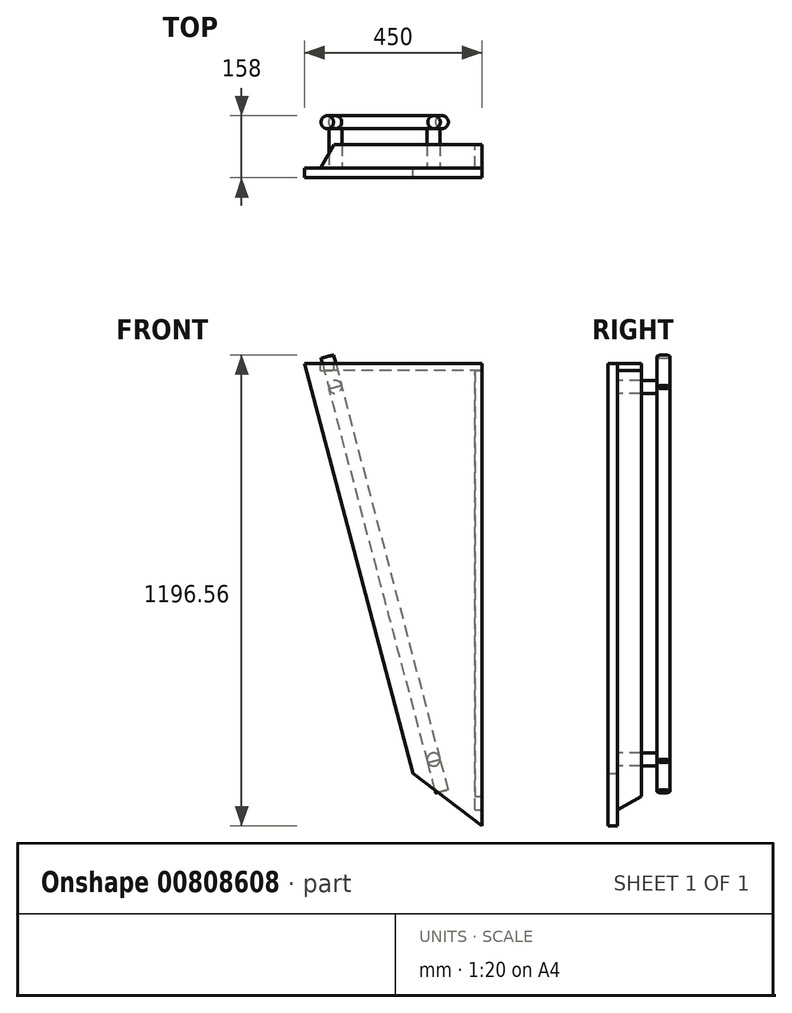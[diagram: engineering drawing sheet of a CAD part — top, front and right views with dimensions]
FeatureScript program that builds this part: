
annotation { "Feature Type Name" : "Feature", "Feature Type Description" : "" }
export const myFeature = defineFeature(function(context is Context, id is Id, definition is map)
    precondition{}
    {
        {
            var Q0;
            Q0=qCreatedBy(makeId("Front.planeOp"),FACE);
            var sketch = newSketch(context, id + "F0", { "sketchPlane" : qUnion([Q0])});
            skLineSegment(sketch, "E0", {"start": v(0, 0) * mm, "end": v(0, 1175) * mm});
            skLineSegment(sketch, "E1", {"start": v(0, 1175) * mm, "end": v(-450, 1175) * mm});
            skLineSegment(sketch, "E2", {"start": v(-450, 1175) * mm, "end": v(-175, 133.32) * mm});
            skLineSegment(sketch, "E3", {"start": v(-175, 133.32) * mm, "end": v(0, 0) * mm});
            skLineSegment(sketch, "E4", {"start": v(-175, 1175) * mm, "end": v(-175, 133.32) * mm, "construction": true});
            skSolve(sketch);
        }
        {
            var Q0;
            Q0 = qSketchRegion(id + "F0", true);
            extrude(context, id + "F1", {"entities" : qUnion([Q0]), "depth" : 25 * mm, "offsetDistance" : 25 * mm});
        }
        {
            var Q0;
            Q0=makeQuery(id+"F1.opExtrude","CAP_FACE",FACE,{"disambiguationData":[OSD([sQuery(id+"F0.wireOp",EDGE,"E0"),sQuery(id+"F0.wireOp",EDGE,"E1"),sQuery(id+"F0.wireOp",EDGE,"E2"),sQuery(id+"F0.wireOp",EDGE,"E3")])],"isStart":true});
            var sketch = newSketch(context, id + "F2", { "sketchPlane" : qUnion([Q0])});
            skLineSegment(sketch, "E5", {"start": v(372.1, 1115) * mm, "end": v(122.25, 168.56) * mm, "construction": true});
            skCircle(sketch, "E6", {"center": v(372.1, 1115) * mm, "radius": 60 * mm, "construction": true});
            skCircle(sketch, "E7", {"center": v(122.25, 168.56) * mm, "radius": 60 * mm, "construction": true});
            skCircle(sketch, "E8", {"center": v(372.1, 1115) * mm, "radius": 30 * mm});
            skCircle(sketch, "E9", {"center": v(122.25, 168.56) * mm, "radius": 30 * mm});
            skCircle(sketch, "E10", {"center": v(372.1, 1115) * mm, "radius": 16.5 * mm});
            skCircle(sketch, "E11", {"center": v(122.25, 168.56) * mm, "radius": 16.5 * mm});
            skSolve(sketch);
        }
        {
            var Q0;
            Q0=makeQuery(id+"F2.imprint","IMPRINT",FACE,{"disambiguationData":[TD([[makeQuery(id+"F2.imprint","IMPRINT",EDGE,{"derivedFrom":sQuery(id+"F2.wireOp",EDGE,"E10")}),1.0]])]});
            var Q1;
            Q1=makeQuery(id+"F2.imprint","IMPRINT",FACE,{"disambiguationData":[TD([[makeQuery(id+"F2.imprint","IMPRINT",EDGE,{"derivedFrom":sQuery(id+"F2.wireOp",EDGE,"E11")}),1.0]])]});
            extrude(context, id + "F3", {"entities" : qUnion([Q0, Q1]), "operationType" : NewBodyOperationType.ADD, "depth" : 100 * mm, "offsetDistance" : 25 * mm});
        }
        {
            var Q0;
            Q0=makeQuery(id+"F3.opExtrude","CAP_FACE",FACE,{"disambiguationData":[OSD([sQuery(id+"F2.wireOp",EDGE,"E10")])],"isStart":false});
            var sketch = newSketch(context, id + "F4", { "sketchPlane" : qUnion([Q0])});
            skLineSegment(sketch, "E12", {"start": v(372.1, 1115) * mm, "end": v(122.25, 168.56) * mm});
            skSolve(sketch);
        }
        {
            var Q0;
            Q0=sQuery(id+"F4.wireOp",VERTEX,"E12.start");
            var Q1;
            Q1=sQuery(id+"F4.wireOp",EDGE,"E12");
            cPlane(context, id + "F5", {"entities" : qUnion([Q0, Q1]), "cplaneType" : CPlaneType.LINE_POINT, "offset" : 25 * mm, "width" : 150 * mm, "height" : 150 * mm});
        }
        {
            var Q0;
            Q0=qCreatedBy(id+"F5.planeOp",FACE);
            var sketch = newSketch(context, id + "F6", { "sketchPlane" : qUnion([Q0])});
            skCircle(sketch, "E13", {"center": v(-75.17, -116.5) * mm, "radius": 16.5 * mm});
            skSolve(sketch);
        }
        {
            var Q0;
            Q0 = qSketchRegion(id + "F6", true);
            extrude(context, id + "F7", {"entities" : qUnion([Q0]), "operationType" : NewBodyOperationType.ADD, "depth" : 982.5 * mm, "offsetDistance" : 25 * mm});
        }
        {
            var Q0;
            Q0=makeQuery(id+"F7.opExtrude","CAP_FACE",FACE,{"disambiguationData":[OSD([sQuery(id+"F6.wireOp",EDGE,"E13")])],"isStart":true});
            extrude(context, id + "F8", {"entities" : qUnion([Q0]), "depth" : 80 * mm, "offsetDistance" : 25 * mm});
        }
        {
            var Q0;
            Q0=makeQuery(id+"F7.opExtrude","CAP_FACE",FACE,{"disambiguationData":[OSD([sQuery(id+"F6.wireOp",EDGE,"E13")])],"isStart":false});
            extrude(context, id + "F9", {"entities" : qUnion([Q0]), "depth" : 80 * mm, "offsetDistance" : 25 * mm});
        }
        {
            var Q0;
            Q0=makeQuery(id+"F1.opExtrude","SWEPT_FACE",FACE,{"disambiguationData":[OSD([sQuery(id+"F0.wireOp",EDGE,"E1")])]});
            var sketch = newSketch(context, id + "F10", { "sketchPlane" : qUnion([Q0])});
            skLineSegment(sketch, "E14.bottom", {"start": v(0, 0) * mm, "end": v(-410, 0) * mm});
            skLineSegment(sketch, "E14.top", {"start": v(0, 60) * mm, "end": v(-375.36, 60) * mm});
            skLineSegment(sketch, "E14.left", {"start": v(0, 0) * mm, "end": v(0, 60) * mm});
            skLineSegment(sketch, "E14.right", {"start": v(-410, 0) * mm, "end": v(-375.36, 60) * mm});
            skSolve(sketch);
        }
        {
            var Q0;
            Q0 = qSketchRegion(id + "F10", true);
            extrude(context, id + "F11", {"entities" : qUnion([Q0]), "oppositeDirection" : true, "depth" : 18 * mm, "offsetDistance" : 25 * mm});
        }
        {
            var Q0;
            Q0=makeQuery(id+"F1.opExtrude","SWEPT_FACE",FACE,{"disambiguationData":[OSD([sQuery(id+"F0.wireOp",EDGE,"E0")])]});
            var sketch = newSketch(context, id + "F12", { "sketchPlane" : qUnion([Q0])});
            skLineSegment(sketch, "E15.bottom", {"start": v(0, 1157) * mm, "end": v(60, 1157) * mm});
            skLineSegment(sketch, "E15.top", {"start": v(0, 40) * mm, "end": v(60, 74.64) * mm});
            skLineSegment(sketch, "E15.left", {"start": v(0, 1157) * mm, "end": v(0, 40) * mm});
            skLineSegment(sketch, "E15.right", {"start": v(60, 1157) * mm, "end": v(60, 74.64) * mm});
            skSolve(sketch);
        }
        {
            var Q0;
            Q0 = qSketchRegion(id + "F12", true);
            extrude(context, id + "F13", {"entities" : qUnion([Q0]), "oppositeDirection" : true, "depth" : 18 * mm, "offsetDistance" : 25 * mm});
        }
    });
